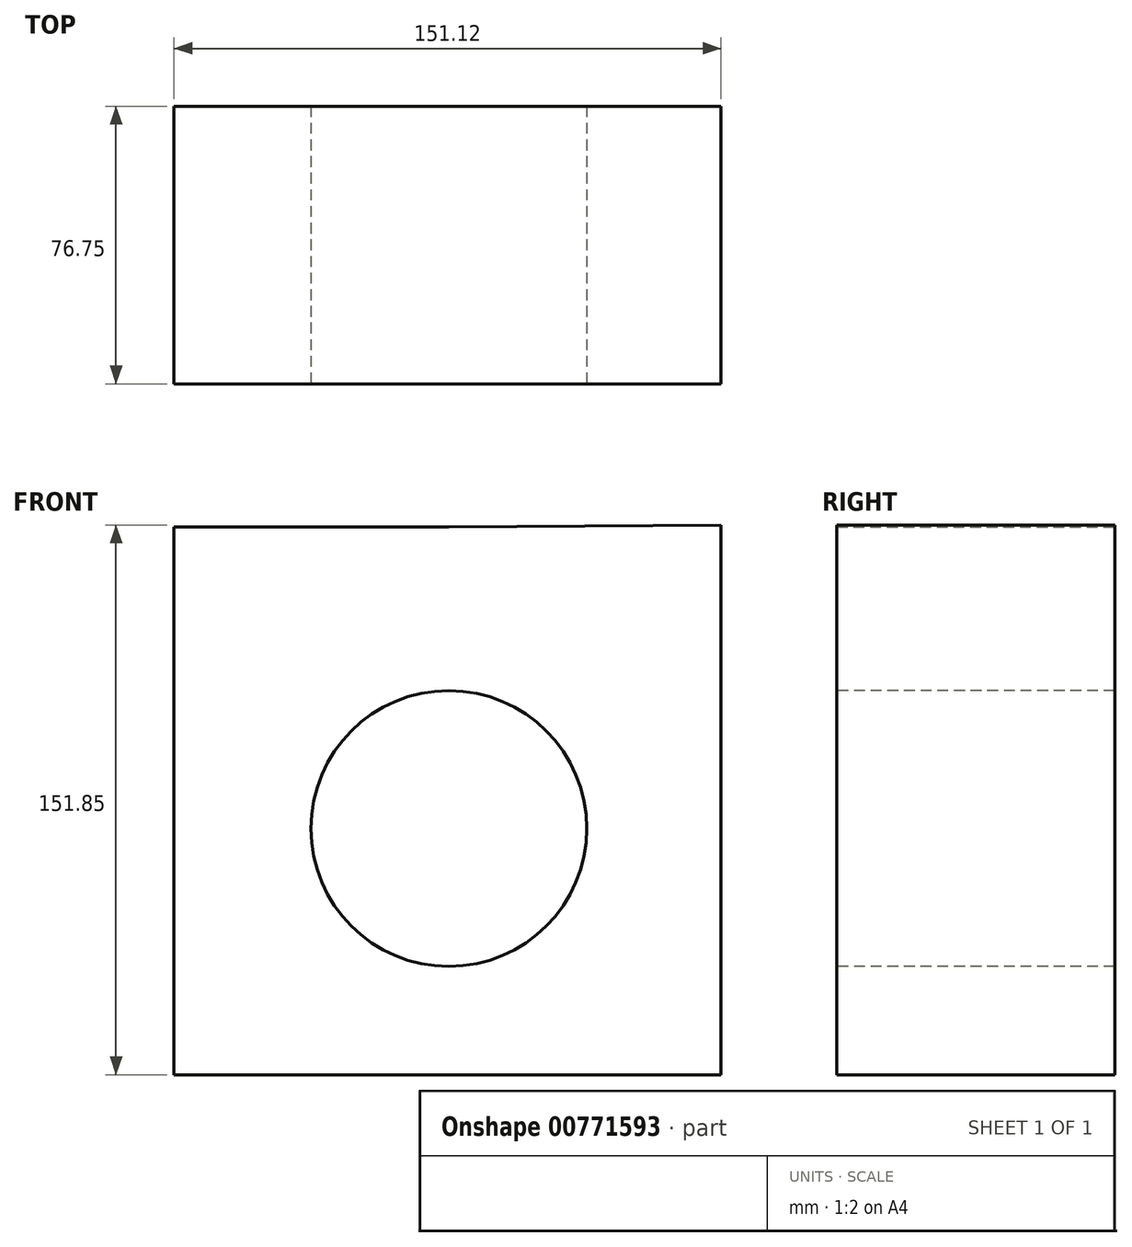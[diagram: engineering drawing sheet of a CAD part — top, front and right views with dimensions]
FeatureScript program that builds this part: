
annotation { "Feature Type Name" : "Feature", "Feature Type Description" : "" }
export const myFeature = defineFeature(function(context is Context, id is Id, definition is map)
    precondition{}
    {
        {
            var Q0;
            Q0=qCreatedBy(makeId("Front.planeOp"),FACE);
            var sketch = newSketch(context, id + "F0", { "sketchPlane" : qUnion([Q0])});
            skLineSegment(sketch, "E0", {"start": v(0, 76.16) * mm, "end": v(-75.91, 76.16) * mm});
            skLineSegment(sketch, "E1", {"start": v(-75.91, 76.16) * mm, "end": v(-75.91, -75.18) * mm});
            skLineSegment(sketch, "E2", {"start": v(-75.91, -75.18) * mm, "end": v(75.2, -75.18) * mm});
            skLineSegment(sketch, "E3", {"start": v(75.2, -75.18) * mm, "end": v(75.2, 76.67) * mm});
            skLineSegment(sketch, "E4", {"start": v(75.2, 76.67) * mm, "end": v(0, 76.16) * mm});
            skSolve(sketch);
        }
        {
            var Q0;
            Q0 = qSketchRegion(id + "F0", true);
            extrude(context, id + "F1", {"entities" : qUnion([Q0]), "depth" : 76.75 * mm, "offsetDistance" : 25.4 * mm});
        }
        {
            var Q0;
            Q0=makeQuery(id+"F1.opExtrude","CAP_FACE",FACE,{"disambiguationData":[OSD([sQuery(id+"F0.wireOp",EDGE,"E0"),sQuery(id+"F0.wireOp",EDGE,"E1"),sQuery(id+"F0.wireOp",EDGE,"E2"),sQuery(id+"F0.wireOp",EDGE,"E3"),sQuery(id+"F0.wireOp",EDGE,"E4")])],"isStart":false});
            var sketch = newSketch(context, id + "F2", { "sketchPlane" : qUnion([Q0])});
            skCircle(sketch, "E5", {"center": v(0, -7.16) * mm, "radius": 30.73 * mm});
            skSolve(sketch);
        }
        {
            var Q0;
            Q0=sQuery(id+"F2.wireOp",VERTEX,"E5.center");
            var Q1;
            Q1=makeQuery(id+"F1.opExtrude","SWEPT_BODY",BODY,{"disambiguationData":[OSD([sQuery(id+"F0.wireOp",EDGE,"E0"),sQuery(id+"F0.wireOp",EDGE,"E1"),sQuery(id+"F0.wireOp",EDGE,"E2"),sQuery(id+"F0.wireOp",EDGE,"E3"),sQuery(id+"F0.wireOp",EDGE,"E4")])]});
            hole(context, id + "F3", {"style" : HoleStyle.SIMPLE, "endStyle" : HoleEndStyle.THROUGH, "holeDiameter" : 76.2 * mm, "majorDiameter" : 6.35 * mm, "isTappedThrough" : true, "tappedDepth" : 12.7 * mm, "tapClearance" : 3, "locations" : qUnion([Q0]), "scope" : qUnion([Q1])});
        }
    });
